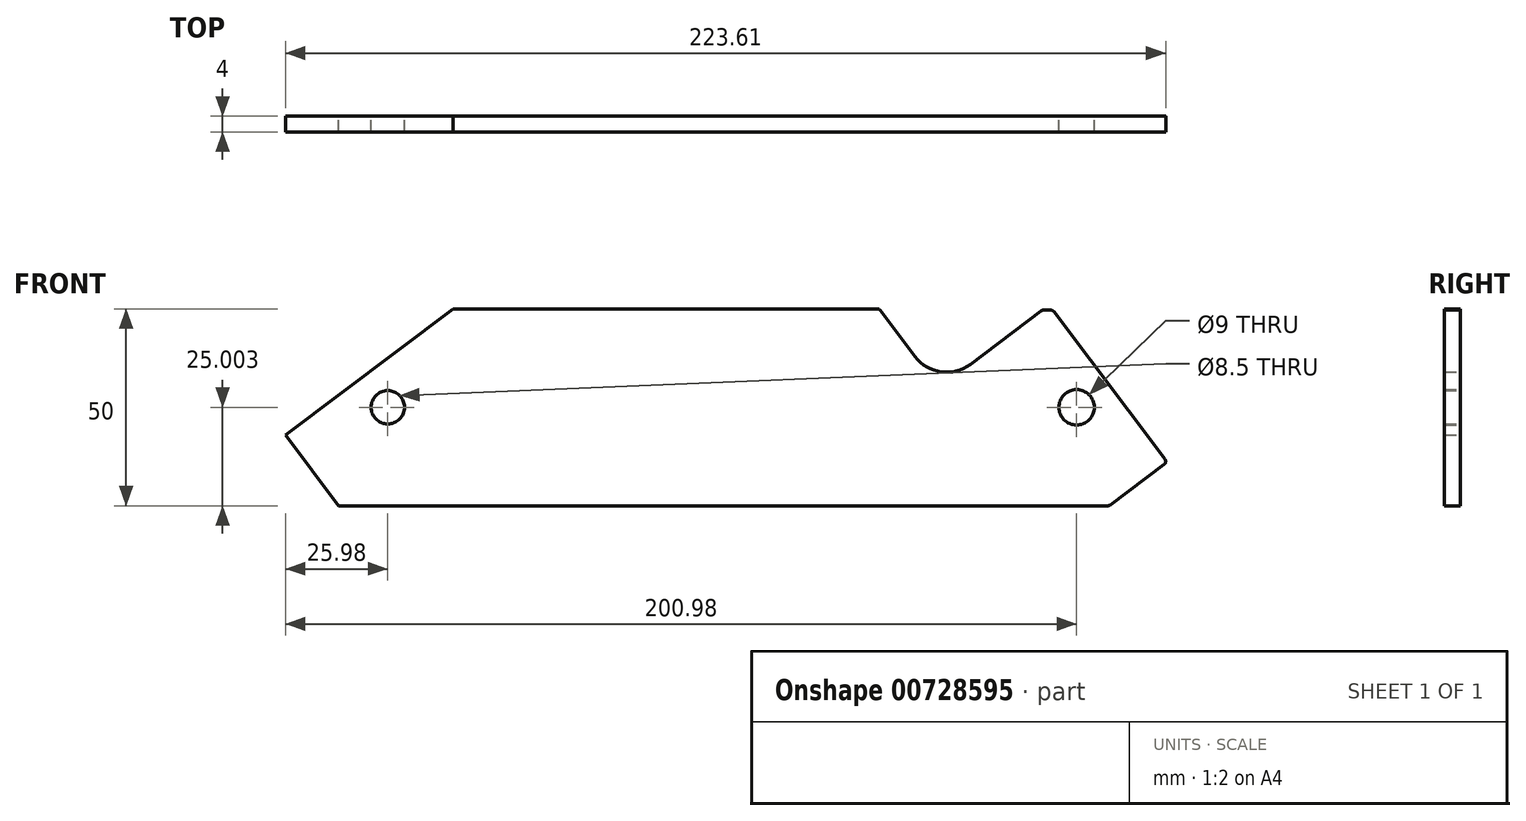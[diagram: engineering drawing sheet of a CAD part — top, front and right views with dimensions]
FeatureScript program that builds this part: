
annotation { "Feature Type Name" : "Feature", "Feature Type Description" : "" }
export const myFeature = defineFeature(function(context is Context, id is Id, definition is map)
    precondition{}
    {
        {
            var Q0;
            Q0=qCreatedBy(makeId("Front.planeOp"),FACE);
            var sketch = newSketch(context, id + "F0", { "sketchPlane" : qUnion([Q0])});
            skCircle(sketch, "E0", {"center": v(-373.15, -207.38) * mm, "radius": 4.25 * mm});
            skCircle(sketch, "E1", {"center": v(-198.15, -207.38) * mm, "radius": 4.5 * mm});
            skLineSegment(sketch, "E2", {"start": v(-190.16, -201.36) * mm, "end": v(-203.93, -183.09) * mm});
            skLineSegment(sketch, "E3", {"start": v(-207.2, -182.89) * mm, "end": v(-225.18, -196.44) * mm});
            skLineSegment(sketch, "E4.MirrorCS", {"start": v(-190.16, -201.36) * mm, "end": v(-175.72, -220.53) * mm});
            skLineSegment(sketch, "E5", {"start": v(-175.92, -221.93) * mm, "end": v(-189.52, -232.18) * mm});
            skLineSegment(sketch, "E6", {"start": v(-356.6, -182.38) * mm, "end": v(-248.8, -182.38) * mm});
            skLineSegment(sketch, "E7.MirrorCS", {"start": v(-385.61, -232.38) * mm, "end": v(-190.12, -232.38) * mm});
            skPoint(sketch, "E8.orphan", {"position": v(-217.2, -232.38) * mm});
            skLineSegment(sketch, "E9", {"start": v(-239.18, -194.47) * mm, "end": v(-248, -182.77) * mm});
            skPoint(sketch, "E10.orphan", {"position": v(-217.2, -182.38) * mm});
            skPoint(sketch, "E11.orphan", {"position": v(-373.71, -232.38) * mm});
            skPoint(sketch, "E12.orphan", {"position": v(-373.71, -182.38) * mm});
            skPoint(sketch, "E13.visualSharp", {"position": v(-233.16, -202.46) * mm});
            skArc(sketch, "E13.filletArc", {"start": v(-239.18, -194.47) * mm, "mid": v(-232.58, -198.35) * mm, "end": v(-225.18, -196.44) * mm});
            skPoint(sketch, "E14.visualSharp", {"position": v(-398.75, -214.15) * mm});
            skArc(sketch, "E14.filletArc", {"start": v(-398.7, -214.22) * mm, "mid": v(-398.7, -214.21) * mm, "end": v(-398.7, -214.2) * mm});
            skPoint(sketch, "E15.visualSharp", {"position": v(-385.02, -232.38) * mm});
            skLineSegment(sketch, "E15.filletArc", {"start": v(-385.02, -232.38) * mm, "end": v(-385.02, -232.38) * mm});
            skPoint(sketch, "E16.visualSharp", {"position": v(-189.79, -232.38) * mm});
            skArc(sketch, "E16.filletArc", {"start": v(-190.12, -232.38) * mm, "mid": v(-189.8, -232.33) * mm, "end": v(-189.52, -232.18) * mm});
            skPoint(sketch, "E17.visualSharp", {"position": v(-175.12, -221.32) * mm});
            skArc(sketch, "E17.filletArc", {"start": v(-175.92, -221.93) * mm, "mid": v(-175.53, -221.27) * mm, "end": v(-175.72, -220.53) * mm});
            skPoint(sketch, "E18.visualSharp", {"position": v(-205.2, -181.4) * mm});
            skPoint(sketch, "E19.visualSharp", {"position": v(-248.3, -182.38) * mm});
            skArc(sketch, "E19.filletArc", {"start": v(-248, -182.77) * mm, "mid": v(-248.34, -182.48) * mm, "end": v(-248.8, -182.38) * mm});
            skPoint(sketch, "E20.visualSharp", {"position": v(-356.59, -182.38) * mm});
            skLineSegment(sketch, "E20.filletArc", {"start": v(-356.25, -182.38) * mm, "end": v(-356.25, -182.38) * mm});
            skLineSegment(sketch, "E21", {"start": v(-288.45, -182.38) * mm, "end": v(-248.26, -182.53) * mm});
            skPoint(sketch, "E22.orphan", {"position": v(-182.5, -182.77) * mm});
            skLineSegment(sketch, "E23.trimOffspring", {"start": v(-206.58, -182.68) * mm, "end": v(-204.73, -182.7) * mm});
            skPoint(sketch, "E24.visualSharp", {"position": v(-206.92, -182.68) * mm});
            skArc(sketch, "E24.filletArc", {"start": v(-206.58, -182.68) * mm, "mid": v(-206.9, -182.74) * mm, "end": v(-207.2, -182.89) * mm});
            skPoint(sketch, "E25.visualSharp", {"position": v(-204.23, -182.7) * mm});
            skArc(sketch, "E25.filletArc", {"start": v(-203.93, -183.09) * mm, "mid": v(-204.28, -182.8) * mm, "end": v(-204.73, -182.7) * mm});
            skLineSegment(sketch, "E26", {"start": v(-399.13, -214.44) * mm, "end": v(-356.6, -182.38) * mm});
            skLineSegment(sketch, "E27", {"start": v(-399.13, -214.44) * mm, "end": v(-385.61, -232.38) * mm});
            skPoint(sketch, "E28.orphan", {"position": v(-379.17, -199.4) * mm});
            skSolve(sketch);
        }
        {
            var Q0;
            Q0 = qSketchRegion(id + "F0", true);
            extrude(context, id + "F1", {"entities" : qUnion([Q0]), "depth" : 4 * mm, "offsetDistance" : 25 * mm});
        }
    });
